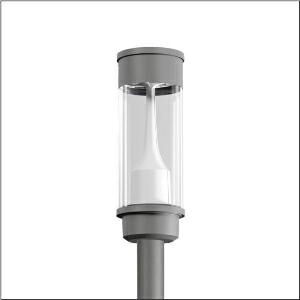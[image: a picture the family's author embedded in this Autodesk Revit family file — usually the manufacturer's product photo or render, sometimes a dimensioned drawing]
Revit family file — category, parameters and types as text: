
# Revit family: litepole_iq___p1_0a_5xa5415lf14h_d8b4
name_source: partatom
category: Lighting Fixtures
units: mm (PartAtom-declared; Revit-internal decimal feet)

## family parameters
Cut with Voids When Loaded = No
Host = Face
Light Source = No
Part Type = Normal
Room Calculation Point = No
Round Connector Dimension = Use Diameter
Shared = No

## types (1)
- --- (1 x LED, 1510 lm, 10 W, 4000K)
    Apparent Load = 10 VA
    CIE Flux Codes = 32 61 90 93 100
    Color Rendering = 70
    Color Temperature = 4000K
    Default Elevation = 1800 mm
    Description = Litepole iQ, mast luminaire, Module 540 iQ-SR, primary light control with 3 zone facetted reflector, of plastic, silver coated, highly specular, structured, primary optical cover: cover, of PMMA, transparent, partly coated, light distribution: P1.0a, light emission: direct distribution, primary light characteristic: strongly asymmetric, installation type: post-top, LED, High Power LED, rated luminous flux: 1.510lm, luminous efficacy: 151lm/W, light colour: 740, colour temperature: 4000K, control gear: ECG iQ, control: optimised constant luminous flux control (CLO 2.0), Desk-Remote (wireless, voltage-free reading and setting of iQ features in the workshop via application-optimized NFC function/RFID function), Light-Fading, Smart-Wire, Night-Set, Lumen-Switch, Temp-Guard, Auto-Match, Street-Remote, presetting dimming logarithmic, with terminal, 6-pole, max. 2.5mm², mains connection: 230..240V, AC, 50/60Hz, start of lifetime: 10W, end of service life: 10W, reduction: 5W, luminaire housing, upper part, of glass-fibre reinforced polyester, coated, Siteco® metallic grey (DB 702S), diameter: 210mm, height: 590mm, spigot size: d x l = 76 x 70mm (post-top) | with reducer (optional accessory) 60 x 70mm, post-top mast mounting element, of diecast aluminium, coated, Siteco® metallic grey (DB 702S), Module 540 iQ-SR, traffic white (RAL 9016), equipment: standard, protection rating (complete): IP65, insulation class (complete): insulation class II (safety insulation), certification: CE, ENEC, VDE, packaging unit: 1 piece

Light Distribution: P1.0a
    Height = 590 mm
    Lamp = 1 x LED
    Lamp Light Flux = 1510 lm
    Lamp Power = 10 W
    Lamp count = 1
    Length = 220 mm
    Luminous efficacy = 151 lm/W
    Manufacturer = Siteco
    ModVariant = No
    Model = 5XA5415LF14H
    Number of Poles = 1
    OnlyDefault = Yes
    Power Factor = 1
    Product Name = Litepole iQ | P1.0a
    Product group = mast luminaire | pylon top
    ProductGroupID = 6100
    Protection Class = Protection class II
    Protection Degree = IP 65
    RLX_Detail_Level = 1
    RLX_Emergency_Light_Flux = 0 lm
    RLX_Emergency_Type = 0
    RLX_Emergency_Type_DB = No
    RlxData = <blob elided: 68273 chars, md5=09ba2d1f>
    Socket = socket
    Standby Power = 0 W
    System Light Flux = 1510 lm
    System Power = 10 W
    Type Comments = factory setting: luminous flux: 100 % | dim-lin: 254 | 401 mA
    Type Image = l_1006025.jpg
    URL = http://relux.com
    VarID = @adj_091021
    Voltage = 0 V
    Weight = 0.00 kg
    Width = 0 mm  [stored 0 ft]

note: [stored X ft] marks values corroborated as IEEE doubles in the binary element streams (Revit-internal decimal feet)

## geometry (parser evidence)
native form markers: Blend x4, Sweep x13
no freeform markers — native parametric forms only
